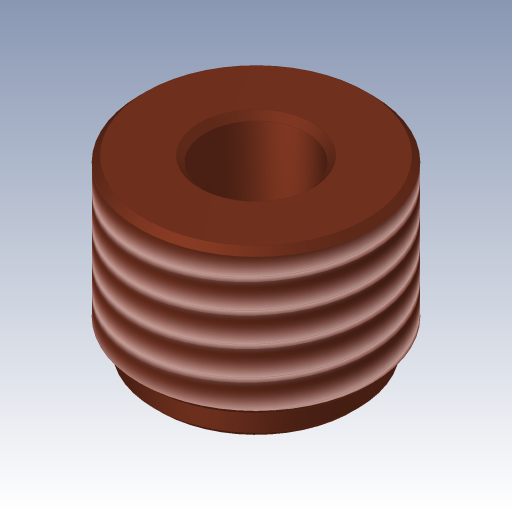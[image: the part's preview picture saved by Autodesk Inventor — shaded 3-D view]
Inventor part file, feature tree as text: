
AUTODESK INVENTOR PART (.ipt)
format: ipt  version: 2023.2 (Build 272271030, 271C)  size: 256,512 bytes
history: native  units: in
note: dims shown in document units (in); Inventor stores cm internally (conversion verified against a paired STEP export)
features: revolve x1, chamfer x1, thread x1, sketch x1
ambient origin geometry x8: Origin, YZ Plane, XZ Plane, XY Plane, X Axis, Y Axis, Z Axis, Center Point
bodies: Body1 (feature_tree)
feature tree (4):
  revolve  "Umdrehung1"
  chamfer  "Fase1"  Distance=0.0591in
  thread  "Gewinde2"  [1 undecoded]
  sketch  "Skizze3"  dims[d4=0.0787in d5=0.0591in d6=0.1378in d8=0.2756in d9=0.315in d10=0.0394in d11=0.2362in d12=90.0deg d13=0.0079in d14=0.0787in d15=45.0deg d18=0.1969in d19=0.0in]
note: 1 required parameter value undecoded (feature->parameter linkage not recoverable at this tier; creation-order binding heuristic only, values carry confidence <= 0.55)
